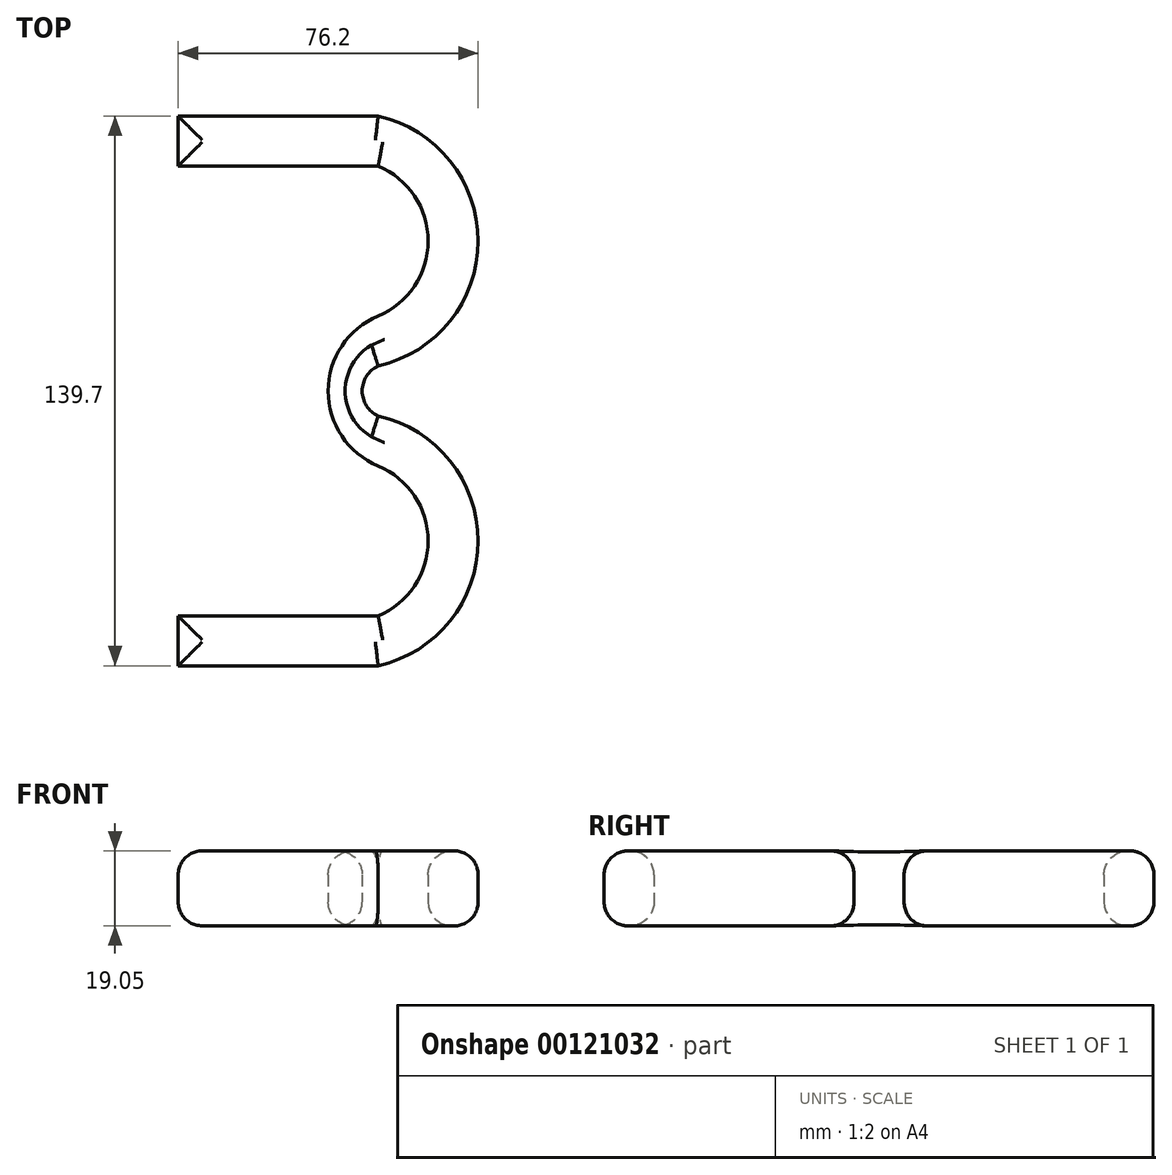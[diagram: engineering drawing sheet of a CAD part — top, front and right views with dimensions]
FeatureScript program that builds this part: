
annotation { "Feature Type Name" : "Feature", "Feature Type Description" : "" }
export const myFeature = defineFeature(function(context is Context, id is Id, definition is map)
    precondition{}
    {
        {
            var Q0;
            Q0=qCreatedBy(makeId("Top.planeOp"),FACE);
            var sketch = newSketch(context, id + "F0", { "sketchPlane" : qUnion([Q0])});
            skLineSegment(sketch, "E0", {"start": v(0, 0) * mm, "end": v(0, 76.2) * mm});
            skArc(sketch, "E1", {"start": v(0, 38.1) * mm, "mid": v(12.7, 57.15) * mm, "end": v(0, 76.2) * mm});
            skArc(sketch, "E2", {"start": v(0, 38.1) * mm, "mid": v(-12.7, 19.05) * mm, "end": v(0, 0) * mm});
            skLineSegment(sketch, "E3", {"start": v(0, 0) * mm, "end": v(0, -76.2) * mm});
            skPoint(sketch, "E4", {"position": v(0, -38.1) * mm});
            skArc(sketch, "E5", {"start": v(0, -38.1) * mm, "mid": v(12.7, -19.05) * mm, "end": v(0, 0) * mm});
            skLineSegment(sketch, "E6", {"start": v(0, 76.2) * mm, "end": v(0, 88.9) * mm});
            skLineSegment(sketch, "E7", {"start": v(0, 38.1) * mm, "end": v(0, 25.4) * mm});
            skLineSegment(sketch, "E8", {"start": v(0, 0) * mm, "end": v(0, 12.7) * mm});
            skLineSegment(sketch, "E9", {"start": v(0, -38.1) * mm, "end": v(0, -50.8) * mm});
            skArc(sketch, "E10", {"start": v(0, -50.8) * mm, "mid": v(25.4, -19.05) * mm, "end": v(0, 12.7) * mm});
            skArc(sketch, "E11", {"start": v(0, 25.4) * mm, "mid": v(25.4, 57.15) * mm, "end": v(0, 88.9) * mm});
            skArc(sketch, "E12", {"start": v(0, 25.4) * mm, "mid": v(-4.06, 19.05) * mm, "end": v(0, 12.7) * mm});
            skPoint(sketch, "E13", {"position": v(0, 88.9) * mm});
            skSolve(sketch);
        }
        {
            var Q0;
            Q0=makeQuery(id+"F0.imprint","IMPRINT",FACE,{"disambiguationData":[TD([[makeQuery(id+"F0.imprint","IMPRINT",EDGE,{"derivedFrom":sQuery(id+"F0.wireOp",EDGE,"E1")}),-1.0]])]});
            var Q1;
            Q1=makeQuery(id+"F0.imprint","IMPRINT",FACE,{"disambiguationData":[TD([[makeQuery(id+"F0.imprint","IMPRINT",EDGE,{"derivedFrom":sQuery(id+"F0.wireOp",EDGE,"E5")}),-1.0]])]});
            var Q2;
            Q2=makeQuery(id+"F0.imprint","IMPRINT",FACE,{"disambiguationData":[TD([[makeQuery(id+"F0.imprint","IMPRINT",EDGE,{"derivedFrom":sQuery(id+"F0.wireOp",EDGE,"E2")}),1.0]])]});
            extrude(context, id + "F1", {"entities" : qUnion([Q0, Q1, Q2]), "depth" : 19.05 * mm});
        }
        {
            var Q0;
            Q0=qCreatedBy(makeId("Top.planeOp"),FACE);
            var sketch = newSketch(context, id + "F2", { "sketchPlane" : qUnion([Q0])});
            skPoint(sketch, "E14", {"position": v(0, 88.9) * mm});
            skLineSegment(sketch, "E15", {"start": v(0, 88.9) * mm, "end": v(-50.8, 88.9) * mm});
            skLineSegment(sketch, "E16", {"start": v(0, -50.8) * mm, "end": v(-50.8, -50.8) * mm});
            skLineSegment(sketch, "E17", {"start": v(0, 76.2) * mm, "end": v(-50.8, 76.2) * mm});
            skLineSegment(sketch, "E18", {"start": v(0, -38.1) * mm, "end": v(-50.8, -38.1) * mm});
            skLineSegment(sketch, "E19", {"start": v(-50.8, -38.1) * mm, "end": v(-50.8, -50.8) * mm});
            skLineSegment(sketch, "E20", {"start": v(-50.8, 76.2) * mm, "end": v(-50.8, 88.9) * mm});
            skLineSegment(sketch, "E21", {"start": v(0, -38.1) * mm, "end": v(0, -50.8) * mm});
            skLineSegment(sketch, "E22", {"start": v(0, 88.9) * mm, "end": v(0, 76.2) * mm});
            skSolve(sketch);
        }
        {
            var Q0;
            Q0 = qSketchRegion(id + "F2", true);
            extrude(context, id + "F3", {"entities" : qUnion([Q0]), "operationType" : NewBodyOperationType.ADD, "depth" : 19.05 * mm});
        }
        {
            var Q0;
            Q0=makeQuery(id+"F3.boolean.opBoolean","MERGE",FACE,{"derivedFrom":[makeQuery(id+"F1.opExtrude","CAP_FACE",FACE,{"disambiguationData":[OSD([sQuery(id+"F0.wireOp",EDGE,"E1"),sQuery(id+"F0.wireOp",EDGE,"E2"),sQuery(id+"F0.wireOp",EDGE,"E5"),sQuery(id+"F0.wireOp",EDGE,"E6"),sQuery(id+"F0.wireOp",EDGE,"E9"),sQuery(id+"F0.wireOp",EDGE,"E10"),sQuery(id+"F0.wireOp",EDGE,"E11"),sQuery(id+"F0.wireOp",EDGE,"E12")])],"isStart":false}),makeQuery(id+"F3.opExtrude","CAP_FACE",FACE,{"disambiguationData":[OSD([sQuery(id+"F2.wireOp",EDGE,"E15"),sQuery(id+"F2.wireOp",EDGE,"E17"),sQuery(id+"F2.wireOp",EDGE,"E20"),sQuery(id+"F2.wireOp",EDGE,"E22")])],"isStart":false}),makeQuery(id+"F3.opExtrude","CAP_FACE",FACE,{"disambiguationData":[OSD([sQuery(id+"F2.wireOp",EDGE,"E16"),sQuery(id+"F2.wireOp",EDGE,"E18"),sQuery(id+"F2.wireOp",EDGE,"E19"),sQuery(id+"F2.wireOp",EDGE,"E21")])],"isStart":false})]});
            var Q1;
            Q1=makeQuery(id+"F3.boolean.opBoolean","MERGE",FACE,{"derivedFrom":[makeQuery(id+"F1.opExtrude","CAP_FACE",FACE,{"disambiguationData":[OSD([sQuery(id+"F0.wireOp",EDGE,"E1"),sQuery(id+"F0.wireOp",EDGE,"E2"),sQuery(id+"F0.wireOp",EDGE,"E5"),sQuery(id+"F0.wireOp",EDGE,"E6"),sQuery(id+"F0.wireOp",EDGE,"E9"),sQuery(id+"F0.wireOp",EDGE,"E10"),sQuery(id+"F0.wireOp",EDGE,"E11"),sQuery(id+"F0.wireOp",EDGE,"E12")])],"isStart":true}),makeQuery(id+"F3.opExtrude","CAP_FACE",FACE,{"disambiguationData":[OSD([sQuery(id+"F2.wireOp",EDGE,"E15"),sQuery(id+"F2.wireOp",EDGE,"E17"),sQuery(id+"F2.wireOp",EDGE,"E20"),sQuery(id+"F2.wireOp",EDGE,"E22")])],"isStart":true}),makeQuery(id+"F3.opExtrude","CAP_FACE",FACE,{"disambiguationData":[OSD([sQuery(id+"F2.wireOp",EDGE,"E16"),sQuery(id+"F2.wireOp",EDGE,"E18"),sQuery(id+"F2.wireOp",EDGE,"E19"),sQuery(id+"F2.wireOp",EDGE,"E21")])],"isStart":true})]});
            fillet(context, id + "F4", {"entities" : qUnion([Q0, Q1]), "radius" : 6.07 * mm, "tangentPropagation" : true, "allowEdgeOverflow" : false});
        }
    });
